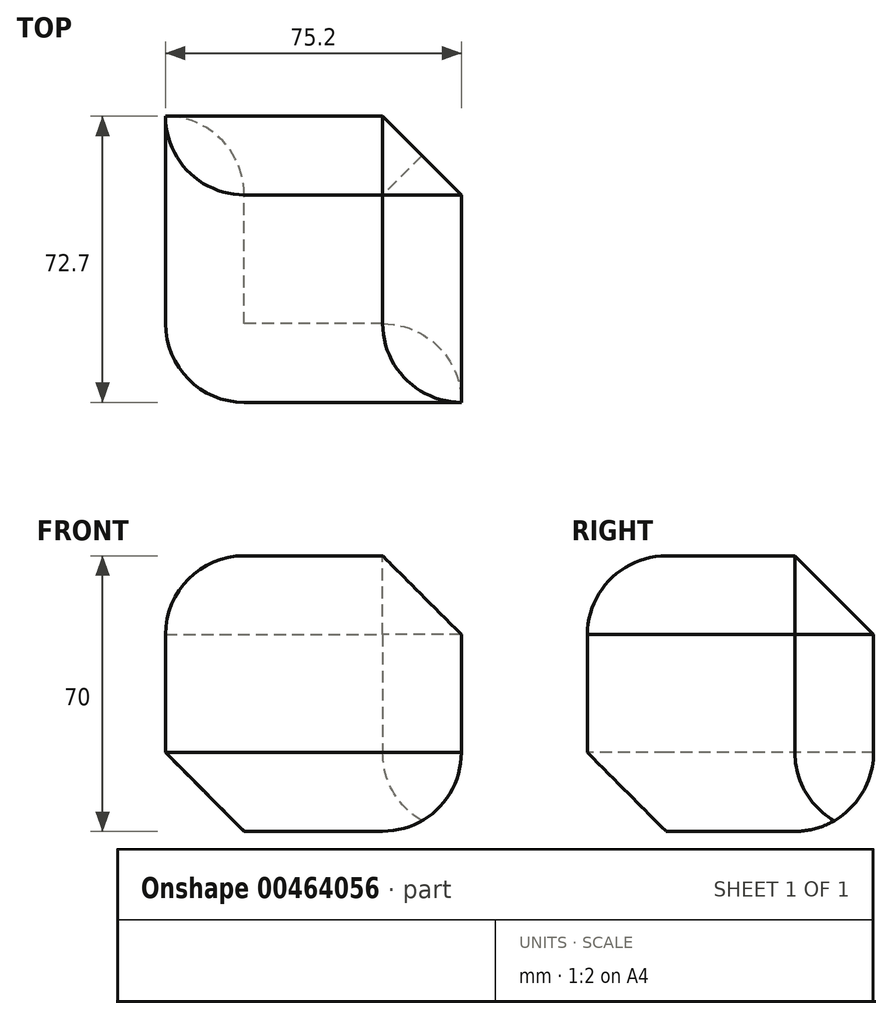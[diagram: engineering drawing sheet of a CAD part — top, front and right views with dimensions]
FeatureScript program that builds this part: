
annotation { "Feature Type Name" : "Feature", "Feature Type Description" : "" }
export const myFeature = defineFeature(function(context is Context, id is Id, definition is map)
    precondition{}
    {
        {
            var Q0;
            Q0=qCreatedBy(makeId("Top.planeOp"),FACE);
            var sketch = newSketch(context, id + "F0", { "sketchPlane" : qUnion([Q0])});
            skLineSegment(sketch, "E0.bottom", {"start": v(37.6, 36.35) * mm, "end": v(-37.6, 36.35) * mm});
            skLineSegment(sketch, "E0.top", {"start": v(37.6, -36.35) * mm, "end": v(-37.6, -36.35) * mm});
            skLineSegment(sketch, "E0.left", {"start": v(37.6, 36.35) * mm, "end": v(37.6, -36.35) * mm});
            skLineSegment(sketch, "E0.right", {"start": v(-37.6, 36.35) * mm, "end": v(-37.6, -36.35) * mm});
            skPoint(sketch, "E0.middle", {"position": v(0, 0) * mm});
            skSolve(sketch);
        }
        {
            var Q0;
            Q0 = qSketchRegion(id + "F0", true);
            extrude(context, id + "F1", {"entities" : qUnion([Q0]), "depth" : 70 * mm});
        }
        {
            var Q0;
            Q0=makeQuery(id+"F1.opExtrude","CAP_EDGE",EDGE,{"disambiguationData":[OSD([sQuery(id+"F0.wireOp",EDGE,"E0.right")])],"isStart":false});
            var Q1;
            Q1=makeQuery(id+"F1.opExtrude","CAP_EDGE",EDGE,{"disambiguationData":[OSD([sQuery(id+"F0.wireOp",EDGE,"E0.top")])],"isStart":false});
            var Q2;
            Q2=makeQuery(id+"F1.opExtrude","SWEPT_EDGE",EDGE,{"disambiguationData":[OSD([sQuery(id+"F0.wireOp",EDGE,"E0.top"),sQuery(id+"F0.wireOp",EDGE,"E0.right")])]});
            var Q3;
            Q3=makeQuery(id+"F1.opExtrude","CAP_EDGE",EDGE,{"disambiguationData":[OSD([sQuery(id+"F0.wireOp",EDGE,"E0.bottom")])],"isStart":true});
            var Q4;
            Q4=makeQuery(id+"F1.opExtrude","CAP_EDGE",EDGE,{"disambiguationData":[OSD([sQuery(id+"F0.wireOp",EDGE,"E0.left")])],"isStart":true});
            fillet(context, id + "F2", {"entities" : qUnion([Q0, Q1, Q2, Q3, Q4]), "radius" : 20 * mm, "tangentPropagation" : true, "allowEdgeOverflow" : false});
        }
        {
            var Q0;
            Q0=makeQuery(id+"F1.opExtrude","CAP_EDGE",EDGE,{"disambiguationData":[OSD([sQuery(id+"F0.wireOp",EDGE,"E0.left")])],"isStart":false});
            var Q1;
            Q1=makeQuery(id+"F1.opExtrude","CAP_EDGE",EDGE,{"disambiguationData":[OSD([sQuery(id+"F0.wireOp",EDGE,"E0.bottom")])],"isStart":false});
            var Q2;
            Q2=makeQuery(id+"F1.opExtrude","SWEPT_EDGE",EDGE,{"disambiguationData":[OSD([sQuery(id+"F0.wireOp",EDGE,"E0.bottom"),sQuery(id+"F0.wireOp",EDGE,"E0.left")])]});
            var Q3;
            Q3=makeQuery(id+"F1.opExtrude","CAP_EDGE",EDGE,{"disambiguationData":[OSD([sQuery(id+"F0.wireOp",EDGE,"E0.top")])],"isStart":true});
            var Q4;
            Q4=makeQuery(id+"F1.opExtrude","CAP_EDGE",EDGE,{"disambiguationData":[OSD([sQuery(id+"F0.wireOp",EDGE,"E0.right")])],"isStart":true});
            chamfer(context, id + "F3", {"entities" : qUnion([Q0, Q1, Q2, Q3, Q4]), "width" : 20 * mm});
        }
    });
